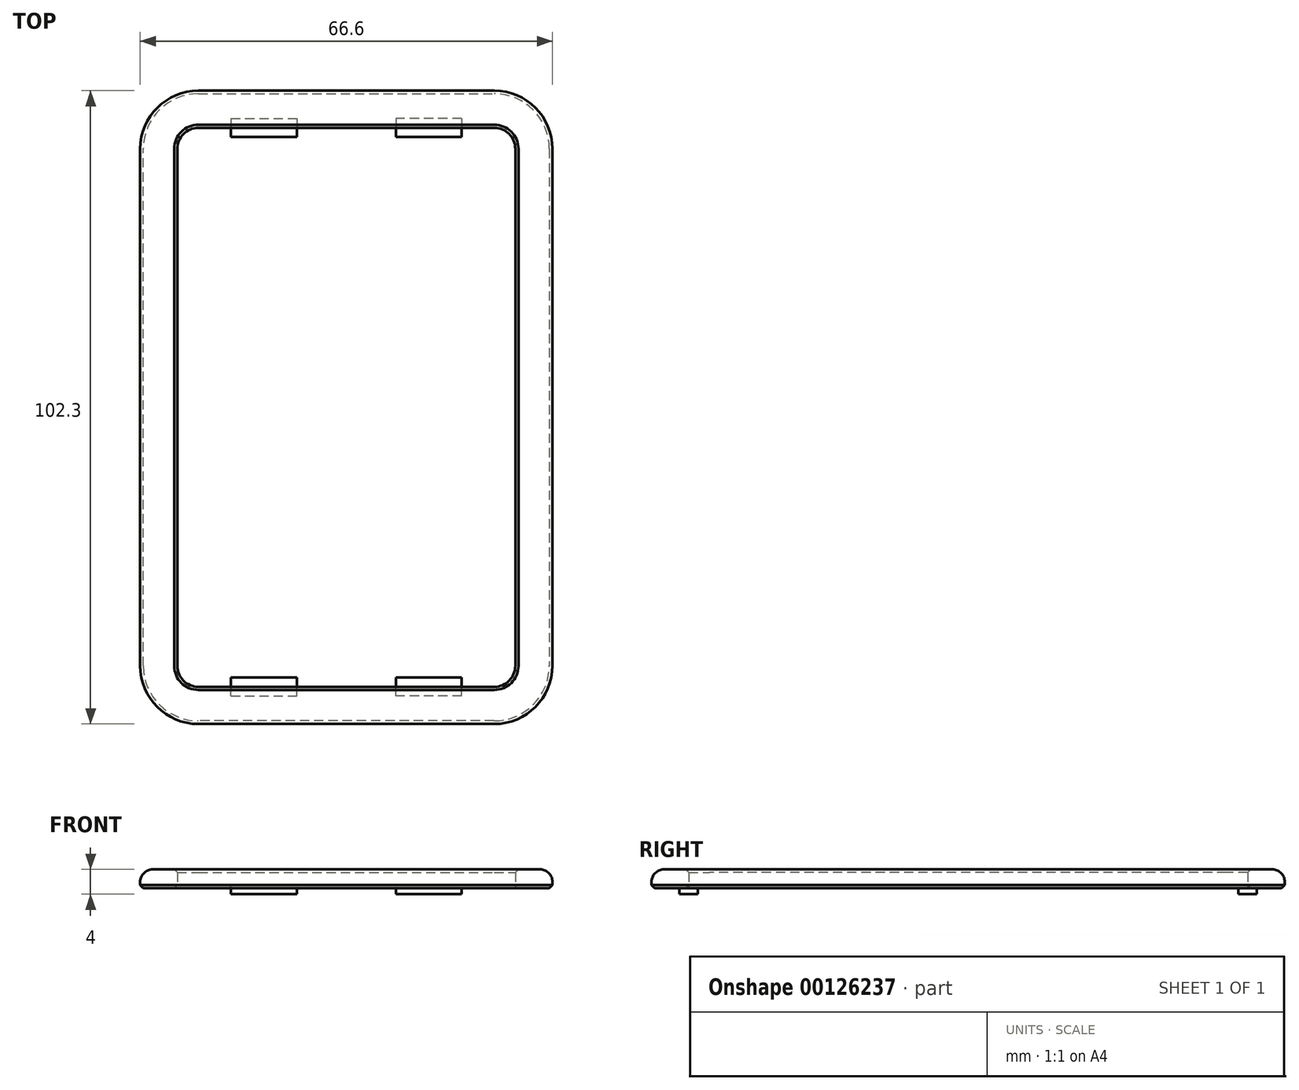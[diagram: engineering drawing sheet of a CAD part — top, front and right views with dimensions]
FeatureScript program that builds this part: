
annotation { "Feature Type Name" : "Feature", "Feature Type Description" : "" }
export const myFeature = defineFeature(function(context is Context, id is Id, definition is map)
    precondition{}
    {
        {
            var Q0;
            Q0=qCreatedBy(makeId("Top.planeOp"),FACE);
            var sketch = newSketch(context, id + "F0", { "sketchPlane" : qUnion([Q0])});
            skLineSegment(sketch, "E0.bottom", {"start": v(23.9, -45.15) * mm, "end": v(-23.9, -45.15) * mm});
            skLineSegment(sketch, "E0.top", {"start": v(23.9, 45.15) * mm, "end": v(-23.9, 45.15) * mm});
            skLineSegment(sketch, "E0.left", {"start": v(27.3, -41.75) * mm, "end": v(27.3, 41.75) * mm});
            skLineSegment(sketch, "E0.right", {"start": v(-27.3, -41.75) * mm, "end": v(-27.3, 41.75) * mm});
            skPoint(sketch, "E0.middle", {"position": v(0, 0) * mm});
            skPoint(sketch, "E1.visualSharp", {"position": v(27.3, 45.15) * mm});
            skArc(sketch, "E1.filletArc", {"start": v(27.3, 41.75) * mm, "mid": v(26.3, 44.15) * mm, "end": v(23.9, 45.15) * mm});
            skPoint(sketch, "E2.visualSharp", {"position": v(27.3, -45.15) * mm});
            skArc(sketch, "E2.filletArc", {"start": v(23.9, -45.15) * mm, "mid": v(26.3, -44.15) * mm, "end": v(27.3, -41.75) * mm});
            skPoint(sketch, "E3.visualSharp", {"position": v(-27.3, -45.15) * mm});
            skArc(sketch, "E3.filletArc", {"start": v(-27.3, -41.75) * mm, "mid": v(-26.3, -44.15) * mm, "end": v(-23.9, -45.15) * mm});
            skPoint(sketch, "E4.visualSharp", {"position": v(-27.3, 45.15) * mm});
            skArc(sketch, "E4.filletArc", {"start": v(-23.9, 45.15) * mm, "mid": v(-26.3, 44.15) * mm, "end": v(-27.3, 41.75) * mm});
            skArc(sketch, "E5.0", {"start": v(-33.3, -41.75) * mm, "mid": v(-30.55, -48.4) * mm, "end": v(-23.9, -51.15) * mm});
            skLineSegment(sketch, "E5.1", {"start": v(23.9, -51.15) * mm, "end": v(-23.9, -51.15) * mm});
            skLineSegment(sketch, "E5.2", {"start": v(-33.3, -41.75) * mm, "end": v(-33.3, 41.75) * mm});
            skArc(sketch, "E5.3", {"start": v(23.9, -51.15) * mm, "mid": v(30.55, -48.4) * mm, "end": v(33.3, -41.75) * mm});
            skArc(sketch, "E5.4", {"start": v(-23.9, 51.15) * mm, "mid": v(-30.55, 48.4) * mm, "end": v(-33.3, 41.75) * mm});
            skLineSegment(sketch, "E5.5", {"start": v(23.9, 51.15) * mm, "end": v(-23.9, 51.15) * mm});
            skArc(sketch, "E5.6", {"start": v(33.3, 41.75) * mm, "mid": v(30.55, 48.4) * mm, "end": v(23.9, 51.15) * mm});
            skLineSegment(sketch, "E5.7", {"start": v(33.3, -41.75) * mm, "end": v(33.3, 41.75) * mm});
            skSolve(sketch);
        }
        {
            var Q0;
            Q0=makeQuery(id+"F0.imprint","IMPRINT",FACE,{"disambiguationData":[TD([[makeQuery(id+"F0.imprint","IMPRINT",EDGE,{"derivedFrom":sQuery(id+"F0.wireOp",EDGE,"E0.bottom")}),1.0]])]});
            extrude(context, id + "F1", {"entities" : qUnion([Q0]), "depth" : 3 * mm});
        }
        {
            var Q0;
            Q0=makeQuery(id+"F1.opExtrude","CAP_EDGE",EDGE,{"disambiguationData":[OSD([sQuery(id+"F0.wireOp",EDGE,"E5.2")])],"isStart":false});
            fillet(context, id + "F2", {"entities" : qUnion([Q0]), "radius" : 2 * mm, "tangentPropagation" : true, "allowEdgeOverflow" : false});
        }
        {
            var Q0;
            Q0=makeQuery(id+"F1.opExtrude","CAP_FACE",FACE,{"disambiguationData":[OSD([sQuery(id+"F0.wireOp",EDGE,"E0.bottom"),sQuery(id+"F0.wireOp",EDGE,"E0.top"),sQuery(id+"F0.wireOp",EDGE,"E0.left"),sQuery(id+"F0.wireOp",EDGE,"E0.right"),sQuery(id+"F0.wireOp",EDGE,"E1.filletArc"),sQuery(id+"F0.wireOp",EDGE,"E2.filletArc"),sQuery(id+"F0.wireOp",EDGE,"E3.filletArc"),sQuery(id+"F0.wireOp",EDGE,"E4.filletArc"),sQuery(id+"F0.wireOp",EDGE,"E5.0"),sQuery(id+"F0.wireOp",EDGE,"E5.1"),sQuery(id+"F0.wireOp",EDGE,"E5.2"),sQuery(id+"F0.wireOp",EDGE,"E5.3"),sQuery(id+"F0.wireOp",EDGE,"E5.4"),sQuery(id+"F0.wireOp",EDGE,"E5.5"),sQuery(id+"F0.wireOp",EDGE,"E5.6"),sQuery(id+"F0.wireOp",EDGE,"E5.7")])],"isStart":true});
            var sketch = newSketch(context, id + "F3", { "sketchPlane" : qUnion([Q0])});
            skLineSegment(sketch, "E6.bottom", {"start": v(-18.64, -46.65) * mm, "end": v(-8, -46.65) * mm});
            skLineSegment(sketch, "E6.top", {"start": v(-18.64, -43.65) * mm, "end": v(-8, -43.65) * mm});
            skLineSegment(sketch, "E6.left", {"start": v(-18.64, -46.65) * mm, "end": v(-18.64, -43.65) * mm});
            skLineSegment(sketch, "E6.right", {"start": v(-8, -46.65) * mm, "end": v(-8, -43.65) * mm});
            skLineSegment(sketch, "E7.MirrorCS", {"start": v(8, -46.65) * mm, "end": v(8, -43.65) * mm});
            skLineSegment(sketch, "E8.MirrorCS", {"start": v(18.64, -46.65) * mm, "end": v(18.64, -43.65) * mm});
            skLineSegment(sketch, "E9.MirrorCS", {"start": v(18.64, -43.65) * mm, "end": v(8, -43.65) * mm});
            skLineSegment(sketch, "E10.MirrorCS", {"start": v(18.64, -46.65) * mm, "end": v(8, -46.65) * mm});
            skLineSegment(sketch, "E11.MirrorCS", {"start": v(-18.64, 46.65) * mm, "end": v(-8, 46.65) * mm});
            skLineSegment(sketch, "E12.MirrorCS", {"start": v(-18.64, 43.65) * mm, "end": v(-8, 43.65) * mm});
            skLineSegment(sketch, "E13.MirrorCS", {"start": v(-18.64, 46.65) * mm, "end": v(-18.64, 43.65) * mm});
            skLineSegment(sketch, "E14.MirrorCS", {"start": v(-8, 46.65) * mm, "end": v(-8, 43.65) * mm});
            skLineSegment(sketch, "E15.MirrorCS", {"start": v(8, 46.65) * mm, "end": v(8, 43.65) * mm});
            skLineSegment(sketch, "E16.MirrorCS", {"start": v(18.64, 46.65) * mm, "end": v(18.64, 43.65) * mm});
            skLineSegment(sketch, "E17.MirrorCS", {"start": v(18.64, 43.65) * mm, "end": v(8, 43.65) * mm});
            skLineSegment(sketch, "E18.MirrorCS", {"start": v(18.64, 46.65) * mm, "end": v(8, 46.65) * mm});
            skSolve(sketch);
        }
        {
            var Q0;
            Q0 = qSketchRegion(id + "F3", true);
            extrude(context, id + "F4", {"entities" : qUnion([Q0]), "operationType" : NewBodyOperationType.ADD, "depth" : 1 * mm});
        }
        {
            var Q0;
            Q0=makeQuery(id+"F1.opExtrude","CAP_EDGE",EDGE,{"disambiguationData":[OSD([sQuery(id+"F0.wireOp",EDGE,"E0.top")])],"isStart":false});
            var Q1;
            Q1=makeQuery(id+"F1.opExtrude","CAP_EDGE",EDGE,{"disambiguationData":[OSD([sQuery(id+"F0.wireOp",EDGE,"E0.right")])],"isStart":true});
            var Q2;
            Q2=makeQuery(id+"F1.opExtrude","CAP_EDGE",EDGE,{"disambiguationData":[OSD([sQuery(id+"F0.wireOp",EDGE,"E5.2")])],"isStart":true});
            chamfer(context, id + "F5", {"entities" : qUnion([Q0, Q1, Q2]), "width" : .5 * mm, "tangentPropagation" : true});
        }
    });
